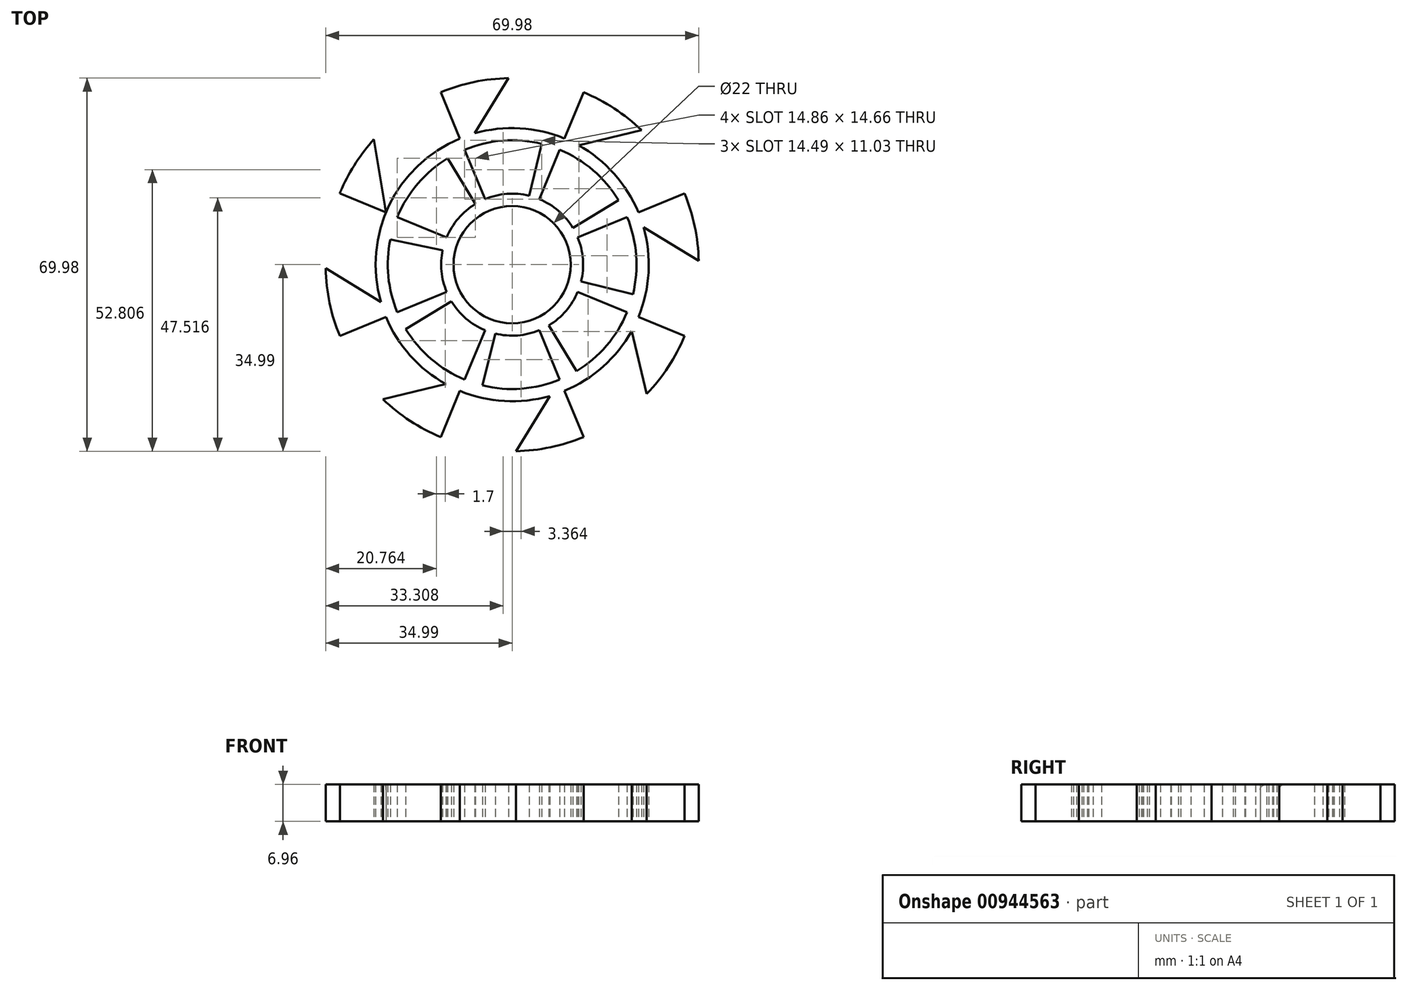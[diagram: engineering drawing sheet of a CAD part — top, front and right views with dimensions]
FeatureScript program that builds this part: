
annotation { "Feature Type Name" : "Feature", "Feature Type Description" : "" }
export const myFeature = defineFeature(function(context is Context, id is Id, definition is map)
    precondition{}
    {
        {
            var Q0;
            Q0=qCreatedBy(makeId("Top.planeOp"),FACE);
            var sketch = newSketch(context, id + "F0", { "sketchPlane" : qUnion([Q0])});
            skCircle(sketch, "E0", {"center": v(0, 0) * mm, "radius": 11 * mm});
            skCircle(sketch, "E1", {"center": v(0, 0) * mm, "radius": 35 * mm});
            skCircle(sketch, "E2", {"center": v(0, 0) * mm, "radius": 13.31 * mm});
            skCircle(sketch, "E3", {"center": v(0, 0) * mm, "radius": 23.33 * mm});
            skCircle(sketch, "E4", {"center": v(0, 0) * mm, "radius": 25.63 * mm});
            skCircle(sketch, "E5.cCircle", {"center": v(0, 0) * mm, "radius": 39.7 * mm, "construction": true});
            skLineSegment(sketch, "E5.0", {"start": v(39.7, 16.44) * mm, "end": v(39.7, -16.44) * mm});
            skLineSegment(sketch, "E5.1", {"start": v(39.7, -16.44) * mm, "end": v(16.44, -39.7) * mm});
            skLineSegment(sketch, "E5.2", {"start": v(16.44, -39.7) * mm, "end": v(-16.44, -39.7) * mm});
            skLineSegment(sketch, "E5.3", {"start": v(-16.44, -39.7) * mm, "end": v(-39.7, -16.44) * mm});
            skLineSegment(sketch, "E5.4", {"start": v(-39.7, -16.44) * mm, "end": v(-39.7, 16.44) * mm});
            skLineSegment(sketch, "E5.5", {"start": v(-39.7, 16.44) * mm, "end": v(-16.44, 39.7) * mm});
            skLineSegment(sketch, "E5.6", {"start": v(-16.44, 39.7) * mm, "end": v(16.44, 39.7) * mm});
            skLineSegment(sketch, "E5.7", {"start": v(16.44, 39.7) * mm, "end": v(39.7, 16.44) * mm});
            skPoint(sketch, "E5.0.midPoint", {"position": v(39.7, 0) * mm});
            skLineSegment(sketch, "E6", {"start": v(0, 0) * mm, "end": v(16.44, 39.7) * mm});
            skLineSegment(sketch, "E7", {"start": v(0, 0) * mm, "end": v(39.7, 16.44) * mm});
            skLineSegment(sketch, "E8", {"start": v(0, 0) * mm, "end": v(39.7, -16.44) * mm});
            skLineSegment(sketch, "E9", {"start": v(-16.44, -39.7) * mm, "end": v(0, 0) * mm});
            skLineSegment(sketch, "E10", {"start": v(-39.7, -16.44) * mm, "end": v(0, 0) * mm});
            skLineSegment(sketch, "E11", {"start": v(-39.7, 16.44) * mm, "end": v(0, 0) * mm});
            skLineSegment(sketch, "E12", {"start": v(-16.44, 39.7) * mm, "end": v(0, 0) * mm});
            skLineSegment(sketch, "E13", {"start": v(16.44, -39.7) * mm, "end": v(0, 0) * mm});
            skLineSegment(sketch, "E14", {"start": v(23.68, 9.8) * mm, "end": v(39.7, 0) * mm});
            skLineSegment(sketch, "E15", {"start": v(23.68, -9.8) * mm, "end": v(28.07, -28.07) * mm});
            skLineSegment(sketch, "E16", {"start": v(9.8, -23.68) * mm, "end": v(0, -39.7) * mm});
            skLineSegment(sketch, "E17", {"start": v(-9.8, -23.68) * mm, "end": v(-28.07, -28.07) * mm});
            skLineSegment(sketch, "E18", {"start": v(-23.68, -9.8) * mm, "end": v(-39.7, 0) * mm});
            skLineSegment(sketch, "E19", {"start": v(-23.68, 9.8) * mm, "end": v(-26.86, 29.22) * mm});
            skLineSegment(sketch, "E20", {"start": v(-9.8, 23.68) * mm, "end": v(0, 39.7) * mm});
            skLineSegment(sketch, "E21", {"start": v(9.8, 23.68) * mm, "end": v(28.07, 28.07) * mm});
            skLineSegment(sketch, "E22", {"start": v(8.93, 21.56) * mm, "end": v(29.6, 26.53) * mm});
            skLineSegment(sketch, "E23", {"start": v(21.56, 8.93) * mm, "end": v(39.63, -2.14) * mm});
            skLineSegment(sketch, "E24", {"start": v(21.56, -8.93) * mm, "end": v(26.5, -29.54) * mm});
            skLineSegment(sketch, "E25", {"start": v(8.93, -21.56) * mm, "end": v(-2.18, -39.7) * mm});
            skLineSegment(sketch, "E26", {"start": v(-8.93, -21.56) * mm, "end": v(-29.54, -26.5) * mm});
            skLineSegment(sketch, "E27", {"start": v(-21.56, -8.93) * mm, "end": v(-39.7, 2.18) * mm});
            skLineSegment(sketch, "E28", {"start": v(-21.56, 8.93) * mm, "end": v(-25.17, 30.97) * mm});
            skLineSegment(sketch, "E29", {"start": v(-8.93, 21.56) * mm, "end": v(2.18, 39.7) * mm});
            skLineSegment(sketch, "E30", {"start": v(0, 39.7) * mm, "end": v(-12.09, 19.96) * mm});
            skLineSegment(sketch, "E31", {"start": v(-12.09, 19.96) * mm, "end": v(0, 0) * mm});
            skLineSegment(sketch, "E32", {"start": v(-26.86, 29.22) * mm, "end": v(-22.85, 4.73) * mm});
            skLineSegment(sketch, "E33", {"start": v(-22.85, 4.73) * mm, "end": v(0, 0) * mm});
            skLineSegment(sketch, "E34", {"start": v(-39.7, 0) * mm, "end": v(-19.96, -12.09) * mm});
            skLineSegment(sketch, "E35", {"start": v(-19.96, -12.09) * mm, "end": v(0, 0) * mm});
            skLineSegment(sketch, "E36", {"start": v(-28.07, -28.07) * mm, "end": v(-5.56, -22.66) * mm});
            skLineSegment(sketch, "E37", {"start": v(-5.56, -22.66) * mm, "end": v(0, 0) * mm});
            skLineSegment(sketch, "E38", {"start": v(0, -39.7) * mm, "end": v(12.09, -19.96) * mm});
            skLineSegment(sketch, "E39", {"start": v(12.09, -19.96) * mm, "end": v(0, 0) * mm});
            skLineSegment(sketch, "E40", {"start": v(28.07, -28.07) * mm, "end": v(22.66, -5.56) * mm});
            skLineSegment(sketch, "E41", {"start": v(22.66, -5.56) * mm, "end": v(0, 0) * mm});
            skLineSegment(sketch, "E42", {"start": v(39.7, 0) * mm, "end": v(19.96, 12.09) * mm});
            skLineSegment(sketch, "E43", {"start": v(19.96, 12.09) * mm, "end": v(0, 0) * mm});
            skLineSegment(sketch, "E44", {"start": v(28.07, 28.07) * mm, "end": v(5.56, 22.66) * mm});
            skLineSegment(sketch, "E45", {"start": v(5.56, 22.66) * mm, "end": v(0, 0) * mm});
            skSolve(sketch);
        }
        {
            var Q0;
            {var subQ0=sQuery(id+"F0.wireOp",EDGE,"E32");var subQ1=sQuery(id+"F0.wireOp",EDGE,"E1");var subQ2=makeQuery(id+"F0.imprint","INTERSECT",VERTEX,{"derivedFrom":[subQ1,subQ0]});Q0=makeQuery(id+"F0.imprint","IMPRINT",FACE,{"disambiguationData":[TD([[makeQuery(id+"F0.imprint","IMPRINT",EDGE,{"disambiguationData":[TD([[subQ2,1.0]])],"derivedFrom":subQ1}),1.0]])]});}
            var Q1;
            {var subQ0=sQuery(id+"F0.wireOp",EDGE,"E29");var subQ5=sQuery(id+"F0.wireOp",EDGE,"E4");var subQ6=makeQuery(id+"F0.imprint","INTERSECT",VERTEX,{"derivedFrom":[subQ5,subQ0]});Q1=makeQuery(id+"F0.imprint","IMPRINT",FACE,{"disambiguationData":[TD([[makeQuery(id+"F0.imprint","IMPRINT",EDGE,{"disambiguationData":[TD([[subQ6,1.0]])],"derivedFrom":subQ5}),1.0]])]});}
            var Q2;
            {var subQ0=sQuery(id+"F0.wireOp",EDGE,"E29");var subQ1=sQuery(id+"F0.wireOp",EDGE,"E1");var subQ2=makeQuery(id+"F0.imprint","INTERSECT",VERTEX,{"derivedFrom":[subQ1,subQ0]});Q2=makeQuery(id+"F0.imprint","IMPRINT",FACE,{"disambiguationData":[TD([[makeQuery(id+"F0.imprint","IMPRINT",EDGE,{"disambiguationData":[TD([[subQ2,-1.0]])],"derivedFrom":subQ1}),1.0]])]});}
            var Q3;
            {var subQ0=sQuery(id+"F0.wireOp",EDGE,"E12");var subQ1=sQuery(id+"F0.wireOp",EDGE,"E3");var subQ2=makeQuery(id+"F0.imprint","INTERSECT",VERTEX,{"derivedFrom":[subQ1,subQ0,sQuery(id+"F0.wireOp",EDGE,"E29")]});Q3=makeQuery(id+"F0.imprint","IMPRINT",FACE,{"disambiguationData":[TD([[makeQuery(id+"F0.imprint","IMPRINT",EDGE,{"disambiguationData":[TD([[subQ2,-1.0]])],"derivedFrom":subQ1}),-1.0]])]});}
            var Q4;
            {var subQ0=sQuery(id+"F0.wireOp",EDGE,"E28");var subQ5=sQuery(id+"F0.wireOp",EDGE,"E4");var subQ6=makeQuery(id+"F0.imprint","INTERSECT",VERTEX,{"derivedFrom":[subQ5,subQ0]});Q4=makeQuery(id+"F0.imprint","IMPRINT",FACE,{"disambiguationData":[TD([[makeQuery(id+"F0.imprint","IMPRINT",EDGE,{"disambiguationData":[TD([[subQ6,1.0]])],"derivedFrom":subQ5}),1.0]])]});}
            var Q5;
            {var subQ0=sQuery(id+"F0.wireOp",EDGE,"E29");var subQ1=sQuery(id+"F0.wireOp",EDGE,"E4");var subQ2=makeQuery(id+"F0.imprint","INTERSECT",VERTEX,{"derivedFrom":[subQ1,subQ0]});Q5=makeQuery(id+"F0.imprint","IMPRINT",FACE,{"disambiguationData":[TD([[makeQuery(id+"F0.imprint","IMPRINT",EDGE,{"disambiguationData":[TD([[subQ2,-1.0]])],"derivedFrom":subQ1}),1.0]])]});}
            var Q6;
            {var subQ0=sQuery(id+"F0.wireOp",EDGE,"E28");var subQ1=sQuery(id+"F0.wireOp",EDGE,"E4");var subQ2=makeQuery(id+"F0.imprint","INTERSECT",VERTEX,{"derivedFrom":[subQ1,subQ0]});Q6=makeQuery(id+"F0.imprint","IMPRINT",FACE,{"disambiguationData":[TD([[makeQuery(id+"F0.imprint","IMPRINT",EDGE,{"disambiguationData":[TD([[subQ2,-1.0]])],"derivedFrom":subQ1}),1.0]])]});}
            var Q7;
            {var subQ0=sQuery(id+"F0.wireOp",EDGE,"E11");var subQ1=sQuery(id+"F0.wireOp",EDGE,"E3");var subQ2=makeQuery(id+"F0.imprint","INTERSECT",VERTEX,{"derivedFrom":[subQ1,subQ0,sQuery(id+"F0.wireOp",EDGE,"E28")]});Q7=makeQuery(id+"F0.imprint","IMPRINT",FACE,{"disambiguationData":[TD([[makeQuery(id+"F0.imprint","IMPRINT",EDGE,{"disambiguationData":[TD([[subQ2,-1.0]])],"derivedFrom":subQ1}),-1.0]])]});}
            var Q8;
            {var subQ0=sQuery(id+"F0.wireOp",EDGE,"E27");var subQ5=sQuery(id+"F0.wireOp",EDGE,"E4");var subQ6=makeQuery(id+"F0.imprint","INTERSECT",VERTEX,{"derivedFrom":[subQ5,subQ0]});Q8=makeQuery(id+"F0.imprint","IMPRINT",FACE,{"disambiguationData":[TD([[makeQuery(id+"F0.imprint","IMPRINT",EDGE,{"disambiguationData":[TD([[subQ6,1.0]])],"derivedFrom":subQ5}),1.0]])]});}
            var Q9;
            {var subQ0=sQuery(id+"F0.wireOp",EDGE,"E27");var subQ1=sQuery(id+"F0.wireOp",EDGE,"E4");var subQ2=makeQuery(id+"F0.imprint","INTERSECT",VERTEX,{"derivedFrom":[subQ1,subQ0]});Q9=makeQuery(id+"F0.imprint","IMPRINT",FACE,{"disambiguationData":[TD([[makeQuery(id+"F0.imprint","IMPRINT",EDGE,{"disambiguationData":[TD([[subQ2,-1.0]])],"derivedFrom":subQ1}),1.0]])]});}
            var Q10;
            {var subQ0=sQuery(id+"F0.wireOp",EDGE,"E10");var subQ1=sQuery(id+"F0.wireOp",EDGE,"E3");var subQ2=makeQuery(id+"F0.imprint","INTERSECT",VERTEX,{"derivedFrom":[subQ1,subQ0,sQuery(id+"F0.wireOp",EDGE,"E27")]});Q10=makeQuery(id+"F0.imprint","IMPRINT",FACE,{"disambiguationData":[TD([[makeQuery(id+"F0.imprint","IMPRINT",EDGE,{"disambiguationData":[TD([[subQ2,-1.0]])],"derivedFrom":subQ1}),-1.0]])]});}
            var Q11;
            {var subQ0=sQuery(id+"F0.wireOp",EDGE,"E26");var subQ5=sQuery(id+"F0.wireOp",EDGE,"E4");var subQ7=makeQuery(id+"F0.imprint","INTERSECT",VERTEX,{"derivedFrom":[subQ5,subQ0]});Q11=makeQuery(id+"F0.imprint","IMPRINT",FACE,{"disambiguationData":[TD([[makeQuery(id+"F0.imprint","IMPRINT",EDGE,{"disambiguationData":[TD([[subQ7,1.0]])],"derivedFrom":subQ5}),1.0]])]});}
            var Q12;
            {var subQ0=sQuery(id+"F0.wireOp",EDGE,"E9");var subQ1=sQuery(id+"F0.wireOp",EDGE,"E3");var subQ2=makeQuery(id+"F0.imprint","INTERSECT",VERTEX,{"derivedFrom":[subQ1,subQ0,sQuery(id+"F0.wireOp",EDGE,"E26")]});Q12=makeQuery(id+"F0.imprint","IMPRINT",FACE,{"disambiguationData":[TD([[makeQuery(id+"F0.imprint","IMPRINT",EDGE,{"disambiguationData":[TD([[subQ2,-1.0]])],"derivedFrom":subQ1}),-1.0]])]});}
            var Q13;
            {var subQ0=sQuery(id+"F0.wireOp",EDGE,"E26");var subQ1=sQuery(id+"F0.wireOp",EDGE,"E4");var subQ2=makeQuery(id+"F0.imprint","INTERSECT",VERTEX,{"derivedFrom":[subQ1,subQ0]});Q13=makeQuery(id+"F0.imprint","IMPRINT",FACE,{"disambiguationData":[TD([[makeQuery(id+"F0.imprint","IMPRINT",EDGE,{"disambiguationData":[TD([[subQ2,-1.0]])],"derivedFrom":subQ1}),1.0]])]});}
            var Q14;
            {var subQ0=sQuery(id+"F0.wireOp",EDGE,"E25");var subQ5=sQuery(id+"F0.wireOp",EDGE,"E4");var subQ6=makeQuery(id+"F0.imprint","INTERSECT",VERTEX,{"derivedFrom":[subQ5,subQ0]});Q14=makeQuery(id+"F0.imprint","IMPRINT",FACE,{"disambiguationData":[TD([[makeQuery(id+"F0.imprint","IMPRINT",EDGE,{"disambiguationData":[TD([[subQ6,1.0]])],"derivedFrom":subQ5}),1.0]])]});}
            var Q15;
            {var subQ0=sQuery(id+"F0.wireOp",EDGE,"E25");var subQ1=sQuery(id+"F0.wireOp",EDGE,"E4");var subQ2=makeQuery(id+"F0.imprint","INTERSECT",VERTEX,{"derivedFrom":[subQ1,subQ0]});Q15=makeQuery(id+"F0.imprint","IMPRINT",FACE,{"disambiguationData":[TD([[makeQuery(id+"F0.imprint","IMPRINT",EDGE,{"disambiguationData":[TD([[subQ2,-1.0]])],"derivedFrom":subQ1}),1.0]])]});}
            var Q16;
            {var subQ0=sQuery(id+"F0.wireOp",EDGE,"E13");var subQ1=sQuery(id+"F0.wireOp",EDGE,"E3");var subQ2=makeQuery(id+"F0.imprint","INTERSECT",VERTEX,{"derivedFrom":[subQ1,subQ0,sQuery(id+"F0.wireOp",EDGE,"E25")]});Q16=makeQuery(id+"F0.imprint","IMPRINT",FACE,{"disambiguationData":[TD([[makeQuery(id+"F0.imprint","IMPRINT",EDGE,{"disambiguationData":[TD([[subQ2,-1.0]])],"derivedFrom":subQ1}),-1.0]])]});}
            var Q17;
            {var subQ0=sQuery(id+"F0.wireOp",EDGE,"E24");var subQ5=sQuery(id+"F0.wireOp",EDGE,"E4");var subQ6=makeQuery(id+"F0.imprint","INTERSECT",VERTEX,{"derivedFrom":[subQ5,subQ0]});Q17=makeQuery(id+"F0.imprint","IMPRINT",FACE,{"disambiguationData":[TD([[makeQuery(id+"F0.imprint","IMPRINT",EDGE,{"disambiguationData":[TD([[subQ6,1.0]])],"derivedFrom":subQ5}),1.0]])]});}
            var Q18;
            {var subQ0=sQuery(id+"F0.wireOp",EDGE,"E8");var subQ1=sQuery(id+"F0.wireOp",EDGE,"E3");var subQ2=makeQuery(id+"F0.imprint","INTERSECT",VERTEX,{"derivedFrom":[subQ1,subQ0,sQuery(id+"F0.wireOp",EDGE,"E24")]});Q18=makeQuery(id+"F0.imprint","IMPRINT",FACE,{"disambiguationData":[TD([[makeQuery(id+"F0.imprint","IMPRINT",EDGE,{"disambiguationData":[TD([[subQ2,-1.0]])],"derivedFrom":subQ1}),-1.0]])]});}
            var Q19;
            {var subQ0=sQuery(id+"F0.wireOp",EDGE,"E24");var subQ1=sQuery(id+"F0.wireOp",EDGE,"E4");var subQ2=makeQuery(id+"F0.imprint","INTERSECT",VERTEX,{"derivedFrom":[subQ1,subQ0]});Q19=makeQuery(id+"F0.imprint","IMPRINT",FACE,{"disambiguationData":[TD([[makeQuery(id+"F0.imprint","IMPRINT",EDGE,{"disambiguationData":[TD([[subQ2,-1.0]])],"derivedFrom":subQ1}),1.0]])]});}
            var Q20;
            {var subQ0=sQuery(id+"F0.wireOp",EDGE,"E23");var subQ5=sQuery(id+"F0.wireOp",EDGE,"E4");var subQ6=makeQuery(id+"F0.imprint","INTERSECT",VERTEX,{"derivedFrom":[subQ5,subQ0]});Q20=makeQuery(id+"F0.imprint","IMPRINT",FACE,{"disambiguationData":[TD([[makeQuery(id+"F0.imprint","IMPRINT",EDGE,{"disambiguationData":[TD([[subQ6,1.0]])],"derivedFrom":subQ5}),1.0]])]});}
            var Q21;
            {var subQ0=sQuery(id+"F0.wireOp",EDGE,"E23");var subQ1=sQuery(id+"F0.wireOp",EDGE,"E4");var subQ2=makeQuery(id+"F0.imprint","INTERSECT",VERTEX,{"derivedFrom":[subQ1,subQ0]});Q21=makeQuery(id+"F0.imprint","IMPRINT",FACE,{"disambiguationData":[TD([[makeQuery(id+"F0.imprint","IMPRINT",EDGE,{"disambiguationData":[TD([[subQ2,-1.0]])],"derivedFrom":subQ1}),1.0]])]});}
            var Q22;
            {var subQ0=sQuery(id+"F0.wireOp",EDGE,"E7");var subQ1=sQuery(id+"F0.wireOp",EDGE,"E3");var subQ2=makeQuery(id+"F0.imprint","INTERSECT",VERTEX,{"derivedFrom":[subQ1,subQ0,sQuery(id+"F0.wireOp",EDGE,"E23")]});Q22=makeQuery(id+"F0.imprint","IMPRINT",FACE,{"disambiguationData":[TD([[makeQuery(id+"F0.imprint","IMPRINT",EDGE,{"disambiguationData":[TD([[subQ2,-1.0]])],"derivedFrom":subQ1}),-1.0]])]});}
            var Q23;
            {var subQ0=sQuery(id+"F0.wireOp",EDGE,"E22");var subQ5=sQuery(id+"F0.wireOp",EDGE,"E4");var subQ6=makeQuery(id+"F0.imprint","INTERSECT",VERTEX,{"derivedFrom":[subQ5,subQ0]});Q23=makeQuery(id+"F0.imprint","IMPRINT",FACE,{"disambiguationData":[TD([[makeQuery(id+"F0.imprint","IMPRINT",EDGE,{"disambiguationData":[TD([[subQ6,1.0]])],"derivedFrom":subQ5}),1.0]])]});}
            var Q24;
            {var subQ0=sQuery(id+"F0.wireOp",EDGE,"E22");var subQ1=sQuery(id+"F0.wireOp",EDGE,"E4");var subQ2=makeQuery(id+"F0.imprint","INTERSECT",VERTEX,{"derivedFrom":[subQ1,subQ0]});Q24=makeQuery(id+"F0.imprint","IMPRINT",FACE,{"disambiguationData":[TD([[makeQuery(id+"F0.imprint","IMPRINT",EDGE,{"disambiguationData":[TD([[subQ2,-1.0]])],"derivedFrom":subQ1}),1.0]])]});}
            var Q25;
            {var subQ0=sQuery(id+"F0.wireOp",EDGE,"E6");var subQ1=sQuery(id+"F0.wireOp",EDGE,"E3");var subQ2=makeQuery(id+"F0.imprint","INTERSECT",VERTEX,{"derivedFrom":[subQ1,subQ0,sQuery(id+"F0.wireOp",EDGE,"E22")]});Q25=makeQuery(id+"F0.imprint","IMPRINT",FACE,{"disambiguationData":[TD([[makeQuery(id+"F0.imprint","IMPRINT",EDGE,{"disambiguationData":[TD([[subQ2,-1.0]])],"derivedFrom":subQ1}),-1.0]])]});}
            var Q26;
            {var subQ0=sQuery(id+"F0.wireOp",EDGE,"E22");var subQ1=sQuery(id+"F0.wireOp",EDGE,"E1");var subQ2=makeQuery(id+"F0.imprint","INTERSECT",VERTEX,{"derivedFrom":[subQ1,subQ0]});Q26=makeQuery(id+"F0.imprint","IMPRINT",FACE,{"disambiguationData":[TD([[makeQuery(id+"F0.imprint","IMPRINT",EDGE,{"disambiguationData":[TD([[subQ2,-1.0]])],"derivedFrom":subQ1}),1.0]])]});}
            var Q27;
            {var subQ0=sQuery(id+"F0.wireOp",EDGE,"E23");var subQ1=sQuery(id+"F0.wireOp",EDGE,"E1");var subQ2=makeQuery(id+"F0.imprint","INTERSECT",VERTEX,{"derivedFrom":[subQ1,subQ0]});Q27=makeQuery(id+"F0.imprint","IMPRINT",FACE,{"disambiguationData":[TD([[makeQuery(id+"F0.imprint","IMPRINT",EDGE,{"disambiguationData":[TD([[subQ2,-1.0]])],"derivedFrom":subQ1}),1.0]])]});}
            var Q28;
            {var subQ0=sQuery(id+"F0.wireOp",EDGE,"E24");var subQ1=sQuery(id+"F0.wireOp",EDGE,"E1");var subQ2=makeQuery(id+"F0.imprint","INTERSECT",VERTEX,{"derivedFrom":[subQ1,subQ0]});Q28=makeQuery(id+"F0.imprint","IMPRINT",FACE,{"disambiguationData":[TD([[makeQuery(id+"F0.imprint","IMPRINT",EDGE,{"disambiguationData":[TD([[subQ2,-1.0]])],"derivedFrom":subQ1}),1.0]])]});}
            var Q29;
            {var subQ0=sQuery(id+"F0.wireOp",EDGE,"E25");var subQ1=sQuery(id+"F0.wireOp",EDGE,"E1");var subQ2=makeQuery(id+"F0.imprint","INTERSECT",VERTEX,{"derivedFrom":[subQ1,subQ0]});Q29=makeQuery(id+"F0.imprint","IMPRINT",FACE,{"disambiguationData":[TD([[makeQuery(id+"F0.imprint","IMPRINT",EDGE,{"disambiguationData":[TD([[subQ2,-1.0]])],"derivedFrom":subQ1}),1.0]])]});}
            var Q30;
            {var subQ0=sQuery(id+"F0.wireOp",EDGE,"E27");var subQ1=sQuery(id+"F0.wireOp",EDGE,"E1");var subQ2=makeQuery(id+"F0.imprint","INTERSECT",VERTEX,{"derivedFrom":[subQ1,subQ0]});Q30=makeQuery(id+"F0.imprint","IMPRINT",FACE,{"disambiguationData":[TD([[makeQuery(id+"F0.imprint","IMPRINT",EDGE,{"disambiguationData":[TD([[subQ2,-1.0]])],"derivedFrom":subQ1}),1.0]])]});}
            var Q31;
            {var subQ0=sQuery(id+"F0.wireOp",EDGE,"E26");var subQ1=sQuery(id+"F0.wireOp",EDGE,"E1");var subQ2=makeQuery(id+"F0.imprint","INTERSECT",VERTEX,{"derivedFrom":[subQ1,subQ0]});Q31=makeQuery(id+"F0.imprint","IMPRINT",FACE,{"disambiguationData":[TD([[makeQuery(id+"F0.imprint","IMPRINT",EDGE,{"disambiguationData":[TD([[subQ2,-1.0]])],"derivedFrom":subQ1}),1.0]])]});}
            var Q32;
            {var subQ0=sQuery(id+"F0.wireOp",EDGE,"E13");var subQ1=sQuery(id+"F0.wireOp",EDGE,"E2");var subQ2=makeQuery(id+"F0.imprint","INTERSECT",VERTEX,{"derivedFrom":[subQ1,subQ0]});Q32=makeQuery(id+"F0.imprint","IMPRINT",FACE,{"disambiguationData":[TD([[makeQuery(id+"F0.imprint","IMPRINT",EDGE,{"disambiguationData":[TD([[subQ2,-1.0]])],"derivedFrom":subQ1}),-1.0]])]});}
            var Q33;
            {var subQ0=sQuery(id+"F0.wireOp",EDGE,"E12");var subQ1=sQuery(id+"F0.wireOp",EDGE,"E2");var subQ2=makeQuery(id+"F0.imprint","INTERSECT",VERTEX,{"derivedFrom":[subQ1,subQ0]});Q33=makeQuery(id+"F0.imprint","IMPRINT",FACE,{"disambiguationData":[TD([[makeQuery(id+"F0.imprint","IMPRINT",EDGE,{"disambiguationData":[TD([[subQ2,-1.0]])],"derivedFrom":subQ1}),-1.0]])]});}
            var Q34;
            {var subQ0=sQuery(id+"F0.wireOp",EDGE,"E6");var subQ1=sQuery(id+"F0.wireOp",EDGE,"E2");var subQ2=makeQuery(id+"F0.imprint","INTERSECT",VERTEX,{"derivedFrom":[subQ1,subQ0]});Q34=makeQuery(id+"F0.imprint","IMPRINT",FACE,{"disambiguationData":[TD([[makeQuery(id+"F0.imprint","IMPRINT",EDGE,{"disambiguationData":[TD([[subQ2,-1.0]])],"derivedFrom":subQ1}),-1.0]])]});}
            var Q35;
            {var subQ0=sQuery(id+"F0.wireOp",EDGE,"E45");var subQ1=sQuery(id+"F0.wireOp",EDGE,"E0");var subQ2=makeQuery(id+"F0.imprint","INTERSECT",VERTEX,{"derivedFrom":[subQ1,subQ0]});Q35=makeQuery(id+"F0.imprint","IMPRINT",FACE,{"disambiguationData":[TD([[makeQuery(id+"F0.imprint","IMPRINT",EDGE,{"disambiguationData":[TD([[subQ2,-1.0]])],"derivedFrom":subQ1}),-1.0]])]});}
            var Q36;
            {var subQ0=sQuery(id+"F0.wireOp",EDGE,"E12");var subQ1=sQuery(id+"F0.wireOp",EDGE,"E0");var subQ2=makeQuery(id+"F0.imprint","INTERSECT",VERTEX,{"derivedFrom":[subQ1,subQ0]});Q36=makeQuery(id+"F0.imprint","IMPRINT",FACE,{"disambiguationData":[TD([[makeQuery(id+"F0.imprint","IMPRINT",EDGE,{"disambiguationData":[TD([[subQ2,-1.0]])],"derivedFrom":subQ1}),-1.0]])]});}
            var Q37;
            {var subQ0=sQuery(id+"F0.wireOp",EDGE,"E11");var subQ1=sQuery(id+"F0.wireOp",EDGE,"E0");var subQ2=makeQuery(id+"F0.imprint","INTERSECT",VERTEX,{"derivedFrom":[subQ1,subQ0]});Q37=makeQuery(id+"F0.imprint","IMPRINT",FACE,{"disambiguationData":[TD([[makeQuery(id+"F0.imprint","IMPRINT",EDGE,{"disambiguationData":[TD([[subQ2,-1.0]])],"derivedFrom":subQ1}),-1.0]])]});}
            var Q38;
            {var subQ0=sQuery(id+"F0.wireOp",EDGE,"E31");var subQ1=sQuery(id+"F0.wireOp",EDGE,"E0");var subQ2=makeQuery(id+"F0.imprint","INTERSECT",VERTEX,{"derivedFrom":[subQ1,subQ0]});Q38=makeQuery(id+"F0.imprint","IMPRINT",FACE,{"disambiguationData":[TD([[makeQuery(id+"F0.imprint","IMPRINT",EDGE,{"disambiguationData":[TD([[subQ2,-1.0]])],"derivedFrom":subQ1}),-1.0]])]});}
            var Q39;
            {var subQ0=sQuery(id+"F0.wireOp",EDGE,"E33");var subQ1=sQuery(id+"F0.wireOp",EDGE,"E0");var subQ2=makeQuery(id+"F0.imprint","INTERSECT",VERTEX,{"derivedFrom":[subQ1,subQ0]});Q39=makeQuery(id+"F0.imprint","IMPRINT",FACE,{"disambiguationData":[TD([[makeQuery(id+"F0.imprint","IMPRINT",EDGE,{"disambiguationData":[TD([[subQ2,-1.0]])],"derivedFrom":subQ1}),-1.0]])]});}
            var Q40;
            {var subQ0=sQuery(id+"F0.wireOp",EDGE,"E35");var subQ1=sQuery(id+"F0.wireOp",EDGE,"E0");var subQ2=makeQuery(id+"F0.imprint","INTERSECT",VERTEX,{"derivedFrom":[subQ1,subQ0]});Q40=makeQuery(id+"F0.imprint","IMPRINT",FACE,{"disambiguationData":[TD([[makeQuery(id+"F0.imprint","IMPRINT",EDGE,{"disambiguationData":[TD([[subQ2,-1.0]])],"derivedFrom":subQ1}),-1.0]])]});}
            var Q41;
            {var subQ0=sQuery(id+"F0.wireOp",EDGE,"E37");var subQ1=sQuery(id+"F0.wireOp",EDGE,"E0");var subQ2=makeQuery(id+"F0.imprint","INTERSECT",VERTEX,{"derivedFrom":[subQ1,subQ0]});Q41=makeQuery(id+"F0.imprint","IMPRINT",FACE,{"disambiguationData":[TD([[makeQuery(id+"F0.imprint","IMPRINT",EDGE,{"disambiguationData":[TD([[subQ2,-1.0]])],"derivedFrom":subQ1}),-1.0]])]});}
            var Q42;
            {var subQ0=sQuery(id+"F0.wireOp",EDGE,"E39");var subQ1=sQuery(id+"F0.wireOp",EDGE,"E0");var subQ2=makeQuery(id+"F0.imprint","INTERSECT",VERTEX,{"derivedFrom":[subQ1,subQ0]});Q42=makeQuery(id+"F0.imprint","IMPRINT",FACE,{"disambiguationData":[TD([[makeQuery(id+"F0.imprint","IMPRINT",EDGE,{"disambiguationData":[TD([[subQ2,-1.0]])],"derivedFrom":subQ1}),-1.0]])]});}
            var Q43;
            {var subQ0=sQuery(id+"F0.wireOp",EDGE,"E7");var subQ1=sQuery(id+"F0.wireOp",EDGE,"E0");var subQ2=makeQuery(id+"F0.imprint","INTERSECT",VERTEX,{"derivedFrom":[subQ1,subQ0]});Q43=makeQuery(id+"F0.imprint","IMPRINT",FACE,{"disambiguationData":[TD([[makeQuery(id+"F0.imprint","IMPRINT",EDGE,{"disambiguationData":[TD([[subQ2,1.0]])],"derivedFrom":subQ1}),-1.0]])]});}
            var Q44;
            {var subQ0=sQuery(id+"F0.wireOp",EDGE,"E43");var subQ1=sQuery(id+"F0.wireOp",EDGE,"E0");var subQ2=makeQuery(id+"F0.imprint","INTERSECT",VERTEX,{"derivedFrom":[subQ1,subQ0]});Q44=makeQuery(id+"F0.imprint","IMPRINT",FACE,{"disambiguationData":[TD([[makeQuery(id+"F0.imprint","IMPRINT",EDGE,{"disambiguationData":[TD([[subQ2,-1.0]])],"derivedFrom":subQ1}),-1.0]])]});}
            var Q45;
            {var subQ0=sQuery(id+"F0.wireOp",EDGE,"E6");var subQ1=sQuery(id+"F0.wireOp",EDGE,"E0");var subQ2=makeQuery(id+"F0.imprint","INTERSECT",VERTEX,{"derivedFrom":[subQ1,subQ0]});Q45=makeQuery(id+"F0.imprint","IMPRINT",FACE,{"disambiguationData":[TD([[makeQuery(id+"F0.imprint","IMPRINT",EDGE,{"disambiguationData":[TD([[subQ2,-1.0]])],"derivedFrom":subQ1}),-1.0]])]});}
            var Q46;
            {var subQ0=sQuery(id+"F0.wireOp",EDGE,"E43");var subQ1=sQuery(id+"F0.wireOp",EDGE,"E0");var subQ2=makeQuery(id+"F0.imprint","INTERSECT",VERTEX,{"derivedFrom":[subQ1,subQ0]});Q46=makeQuery(id+"F0.imprint","IMPRINT",FACE,{"disambiguationData":[TD([[makeQuery(id+"F0.imprint","IMPRINT",EDGE,{"disambiguationData":[TD([[subQ2,1.0]])],"derivedFrom":subQ1}),-1.0]])]});}
            var Q47;
            {var subQ0=sQuery(id+"F0.wireOp",EDGE,"E8");var subQ1=sQuery(id+"F0.wireOp",EDGE,"E0");var subQ2=makeQuery(id+"F0.imprint","INTERSECT",VERTEX,{"derivedFrom":[subQ1,subQ0]});Q47=makeQuery(id+"F0.imprint","IMPRINT",FACE,{"disambiguationData":[TD([[makeQuery(id+"F0.imprint","IMPRINT",EDGE,{"disambiguationData":[TD([[subQ2,-1.0]])],"derivedFrom":subQ1}),-1.0]])]});}
            var Q48;
            {var subQ0=sQuery(id+"F0.wireOp",EDGE,"E13");var subQ1=sQuery(id+"F0.wireOp",EDGE,"E0");var subQ2=makeQuery(id+"F0.imprint","INTERSECT",VERTEX,{"derivedFrom":[subQ1,subQ0]});Q48=makeQuery(id+"F0.imprint","IMPRINT",FACE,{"disambiguationData":[TD([[makeQuery(id+"F0.imprint","IMPRINT",EDGE,{"disambiguationData":[TD([[subQ2,-1.0]])],"derivedFrom":subQ1}),-1.0]])]});}
            var Q49;
            {var subQ0=sQuery(id+"F0.wireOp",EDGE,"E9");var subQ1=sQuery(id+"F0.wireOp",EDGE,"E0");var subQ2=makeQuery(id+"F0.imprint","INTERSECT",VERTEX,{"derivedFrom":[subQ1,subQ0]});Q49=makeQuery(id+"F0.imprint","IMPRINT",FACE,{"disambiguationData":[TD([[makeQuery(id+"F0.imprint","IMPRINT",EDGE,{"disambiguationData":[TD([[subQ2,-1.0]])],"derivedFrom":subQ1}),-1.0]])]});}
            var Q50;
            {var subQ0=sQuery(id+"F0.wireOp",EDGE,"E10");var subQ1=sQuery(id+"F0.wireOp",EDGE,"E0");var subQ2=makeQuery(id+"F0.imprint","INTERSECT",VERTEX,{"derivedFrom":[subQ1,subQ0]});Q50=makeQuery(id+"F0.imprint","IMPRINT",FACE,{"disambiguationData":[TD([[makeQuery(id+"F0.imprint","IMPRINT",EDGE,{"disambiguationData":[TD([[subQ2,-1.0]])],"derivedFrom":subQ1}),-1.0]])]});}
            var Q51;
            {var subQ0=sQuery(id+"F0.wireOp",EDGE,"E9");var subQ1=sQuery(id+"F0.wireOp",EDGE,"E2");var subQ2=makeQuery(id+"F0.imprint","INTERSECT",VERTEX,{"derivedFrom":[subQ1,subQ0]});Q51=makeQuery(id+"F0.imprint","IMPRINT",FACE,{"disambiguationData":[TD([[makeQuery(id+"F0.imprint","IMPRINT",EDGE,{"disambiguationData":[TD([[subQ2,-1.0]])],"derivedFrom":subQ1}),-1.0]])]});}
            var Q52;
            {var subQ0=sQuery(id+"F0.wireOp",EDGE,"E10");var subQ1=sQuery(id+"F0.wireOp",EDGE,"E2");var subQ2=makeQuery(id+"F0.imprint","INTERSECT",VERTEX,{"derivedFrom":[subQ1,subQ0]});Q52=makeQuery(id+"F0.imprint","IMPRINT",FACE,{"disambiguationData":[TD([[makeQuery(id+"F0.imprint","IMPRINT",EDGE,{"disambiguationData":[TD([[subQ2,-1.0]])],"derivedFrom":subQ1}),-1.0]])]});}
            var Q53;
            {var subQ0=sQuery(id+"F0.wireOp",EDGE,"E11");var subQ1=sQuery(id+"F0.wireOp",EDGE,"E2");var subQ2=makeQuery(id+"F0.imprint","INTERSECT",VERTEX,{"derivedFrom":[subQ1,subQ0]});Q53=makeQuery(id+"F0.imprint","IMPRINT",FACE,{"disambiguationData":[TD([[makeQuery(id+"F0.imprint","IMPRINT",EDGE,{"disambiguationData":[TD([[subQ2,-1.0]])],"derivedFrom":subQ1}),-1.0]])]});}
            var Q54;
            {var subQ0=sQuery(id+"F0.wireOp",EDGE,"E8");var subQ1=sQuery(id+"F0.wireOp",EDGE,"E2");var subQ2=makeQuery(id+"F0.imprint","INTERSECT",VERTEX,{"derivedFrom":[subQ1,subQ0]});Q54=makeQuery(id+"F0.imprint","IMPRINT",FACE,{"disambiguationData":[TD([[makeQuery(id+"F0.imprint","IMPRINT",EDGE,{"disambiguationData":[TD([[subQ2,-1.0]])],"derivedFrom":subQ1}),-1.0]])]});}
            var Q55;
            {var subQ0=sQuery(id+"F0.wireOp",EDGE,"E43");var subQ1=sQuery(id+"F0.wireOp",EDGE,"E2");var subQ2=makeQuery(id+"F0.imprint","INTERSECT",VERTEX,{"derivedFrom":[subQ1,subQ0]});Q55=makeQuery(id+"F0.imprint","IMPRINT",FACE,{"disambiguationData":[TD([[makeQuery(id+"F0.imprint","IMPRINT",EDGE,{"disambiguationData":[TD([[subQ2,1.0]])],"derivedFrom":subQ1}),-1.0]])]});}
            extrude(context, id + "F1", {"entities" : qUnion([Q0, Q1, Q2, Q3, Q4, Q5, Q6, Q7, Q8, Q9, Q10, Q11, Q12, Q13, Q14, Q15, Q16, Q17, Q18, Q19, Q20, Q21, Q22, Q23, Q24, Q25, Q26, Q27, Q28, Q29, Q30, Q31, Q32, Q33, Q34, Q35, Q36, Q37, Q38, Q39, Q40, Q41, Q42, Q43, Q44, Q45, Q46, Q47, Q48, Q49, Q50, Q51, Q52, Q53, Q54, Q55]), "depth" : 6.96 * mm, "offsetDistance" : 25 * mm});
        }
        {
            var Q0;
            {var subQ0=sQuery(id+"F0.wireOp",EDGE,"E2");Q0=makeQuery(id+"F1.opExtrude","CAP_EDGE",EDGE,{"disambiguationData":[OSD([subQ0]),TDD([makeQuery(id+"F0.imprint","IMPRINT",EDGE,{"disambiguationData":[TD([[makeQuery(id+"F0.imprint","INTERSECT",VERTEX,{"derivedFrom":[subQ0,sQuery(id+"F0.wireOp",EDGE,"E43")]}),-1.0]])],"derivedFrom":subQ0})])],"isStart":false});}
            var Q1;
            {var subQ0=sQuery(id+"F0.wireOp",EDGE,"E2");Q1=makeQuery(id+"F1.opExtrude","CAP_EDGE",EDGE,{"disambiguationData":[OSD([subQ0]),TDD([makeQuery(id+"F0.imprint","IMPRINT",EDGE,{"disambiguationData":[TD([[makeQuery(id+"F0.imprint","INTERSECT",VERTEX,{"derivedFrom":[subQ0,sQuery(id+"F0.wireOp",EDGE,"E7")]}),1.0]])],"derivedFrom":subQ0})])],"isStart":false});}
            var Q2;
            {var subQ0=sQuery(id+"F0.wireOp",EDGE,"E2");Q2=makeQuery(id+"F1.opExtrude","CAP_EDGE",EDGE,{"disambiguationData":[OSD([subQ0]),TDD([makeQuery(id+"F0.imprint","IMPRINT",EDGE,{"disambiguationData":[TD([[makeQuery(id+"F0.imprint","INTERSECT",VERTEX,{"derivedFrom":[subQ0,sQuery(id+"F0.wireOp",EDGE,"E39")]}),-1.0]])],"derivedFrom":subQ0})])],"isStart":false});}
            var Q3;
            {var subQ0=sQuery(id+"F0.wireOp",EDGE,"E2");Q3=makeQuery(id+"F1.opExtrude","CAP_EDGE",EDGE,{"disambiguationData":[OSD([subQ0]),TDD([makeQuery(id+"F0.imprint","IMPRINT",EDGE,{"disambiguationData":[TD([[makeQuery(id+"F0.imprint","INTERSECT",VERTEX,{"derivedFrom":[subQ0,sQuery(id+"F0.wireOp",EDGE,"E37")]}),-1.0]])],"derivedFrom":subQ0})])],"isStart":false});}
            var Q4;
            {var subQ0=sQuery(id+"F0.wireOp",EDGE,"E2");Q4=makeQuery(id+"F1.opExtrude","CAP_EDGE",EDGE,{"disambiguationData":[OSD([subQ0]),TDD([makeQuery(id+"F0.imprint","IMPRINT",EDGE,{"disambiguationData":[TD([[makeQuery(id+"F0.imprint","INTERSECT",VERTEX,{"derivedFrom":[subQ0,sQuery(id+"F0.wireOp",EDGE,"E35")]}),-1.0]])],"derivedFrom":subQ0})])],"isStart":false});}
            var Q5;
            {var subQ0=sQuery(id+"F0.wireOp",EDGE,"E2");Q5=makeQuery(id+"F1.opExtrude","CAP_EDGE",EDGE,{"disambiguationData":[OSD([subQ0]),TDD([makeQuery(id+"F0.imprint","IMPRINT",EDGE,{"disambiguationData":[TD([[makeQuery(id+"F0.imprint","INTERSECT",VERTEX,{"derivedFrom":[subQ0,sQuery(id+"F0.wireOp",EDGE,"E33")]}),-1.0]])],"derivedFrom":subQ0})])],"isStart":false});}
            var Q6;
            {var subQ0=sQuery(id+"F0.wireOp",EDGE,"E2");Q6=makeQuery(id+"F1.opExtrude","CAP_EDGE",EDGE,{"disambiguationData":[OSD([subQ0]),TDD([makeQuery(id+"F0.imprint","IMPRINT",EDGE,{"disambiguationData":[TD([[makeQuery(id+"F0.imprint","INTERSECT",VERTEX,{"derivedFrom":[subQ0,sQuery(id+"F0.wireOp",EDGE,"E31")]}),-1.0]])],"derivedFrom":subQ0})])],"isStart":false});}
            var Q7;
            {var subQ0=sQuery(id+"F0.wireOp",EDGE,"E2");Q7=makeQuery(id+"F1.opExtrude","CAP_EDGE",EDGE,{"disambiguationData":[OSD([subQ0]),TDD([makeQuery(id+"F0.imprint","IMPRINT",EDGE,{"disambiguationData":[TD([[makeQuery(id+"F0.imprint","INTERSECT",VERTEX,{"derivedFrom":[subQ0,sQuery(id+"F0.wireOp",EDGE,"E45")]}),-1.0]])],"derivedFrom":subQ0})])],"isStart":false});}
            var Q8;
            Q8=makeQuery(id+"F1.opExtrude","CAP_EDGE",EDGE,{"disambiguationData":[OSD([sQuery(id+"F0.wireOp",EDGE,"E45")])],"isStart":false});
            var Q9;
            Q9=makeQuery(id+"F1.opExtrude","CAP_EDGE",EDGE,{"disambiguationData":[OSD([sQuery(id+"F0.wireOp",EDGE,"E6")])],"isStart":false});
            var Q10;
            Q10=makeQuery(id+"F1.opExtrude","CAP_EDGE",EDGE,{"disambiguationData":[OSD([sQuery(id+"F0.wireOp",EDGE,"E43")])],"isStart":false});
            var Q11;
            Q11=makeQuery(id+"F1.opExtrude","CAP_EDGE",EDGE,{"disambiguationData":[OSD([sQuery(id+"F0.wireOp",EDGE,"E7")])],"isStart":false});
            var Q12;
            Q12=makeQuery(id+"F1.opExtrude","CAP_EDGE",EDGE,{"disambiguationData":[OSD([sQuery(id+"F0.wireOp",EDGE,"E41")])],"isStart":false});
            var Q13;
            Q13=makeQuery(id+"F1.opExtrude","CAP_EDGE",EDGE,{"disambiguationData":[OSD([sQuery(id+"F0.wireOp",EDGE,"E8")])],"isStart":false});
            var Q14;
            Q14=makeQuery(id+"F1.opExtrude","CAP_EDGE",EDGE,{"disambiguationData":[OSD([sQuery(id+"F0.wireOp",EDGE,"E39")])],"isStart":false});
            var Q15;
            Q15=makeQuery(id+"F1.opExtrude","CAP_EDGE",EDGE,{"disambiguationData":[OSD([sQuery(id+"F0.wireOp",EDGE,"E13")])],"isStart":false});
            var Q16;
            Q16=makeQuery(id+"F1.opExtrude","CAP_EDGE",EDGE,{"disambiguationData":[OSD([sQuery(id+"F0.wireOp",EDGE,"E37")])],"isStart":false});
            var Q17;
            Q17=makeQuery(id+"F1.opExtrude","CAP_EDGE",EDGE,{"disambiguationData":[OSD([sQuery(id+"F0.wireOp",EDGE,"E9")])],"isStart":false});
            var Q18;
            Q18=makeQuery(id+"F1.opExtrude","CAP_EDGE",EDGE,{"disambiguationData":[OSD([sQuery(id+"F0.wireOp",EDGE,"E35")])],"isStart":false});
            var Q19;
            Q19=makeQuery(id+"F1.opExtrude","CAP_EDGE",EDGE,{"disambiguationData":[OSD([sQuery(id+"F0.wireOp",EDGE,"E10")])],"isStart":false});
            var Q20;
            Q20=makeQuery(id+"F1.opExtrude","CAP_EDGE",EDGE,{"disambiguationData":[OSD([sQuery(id+"F0.wireOp",EDGE,"E33")])],"isStart":false});
            var Q21;
            Q21=makeQuery(id+"F1.opExtrude","CAP_EDGE",EDGE,{"disambiguationData":[OSD([sQuery(id+"F0.wireOp",EDGE,"E11")])],"isStart":false});
            var Q22;
            Q22=makeQuery(id+"F1.opExtrude","CAP_EDGE",EDGE,{"disambiguationData":[OSD([sQuery(id+"F0.wireOp",EDGE,"E31")])],"isStart":false});
            var Q23;
            Q23=makeQuery(id+"F1.opExtrude","CAP_EDGE",EDGE,{"disambiguationData":[OSD([sQuery(id+"F0.wireOp",EDGE,"E12")])],"isStart":false});
            var Q24;
            {var subQ0=sQuery(id+"F0.wireOp",EDGE,"E3");Q24=makeQuery(id+"F1.opExtrude","CAP_EDGE",EDGE,{"disambiguationData":[OSD([subQ0]),TDD([makeQuery(id+"F0.imprint","IMPRINT",EDGE,{"disambiguationData":[TD([[makeQuery(id+"F0.imprint","INTERSECT",VERTEX,{"derivedFrom":[subQ0,sQuery(id+"F0.wireOp",EDGE,"E12"),sQuery(id+"F0.wireOp",EDGE,"E29")]}),1.0]])],"derivedFrom":subQ0})])],"isStart":false});}
            var Q25;
            {var subQ0=sQuery(id+"F0.wireOp",EDGE,"E3");Q25=makeQuery(id+"F1.opExtrude","CAP_EDGE",EDGE,{"disambiguationData":[OSD([subQ0]),TDD([makeQuery(id+"F0.imprint","IMPRINT",EDGE,{"disambiguationData":[TD([[makeQuery(id+"F0.imprint","INTERSECT",VERTEX,{"derivedFrom":[subQ0,sQuery(id+"F0.wireOp",EDGE,"E6"),sQuery(id+"F0.wireOp",EDGE,"E22")]}),1.0]])],"derivedFrom":subQ0})])],"isStart":false});}
            var Q26;
            {var subQ0=sQuery(id+"F0.wireOp",EDGE,"E3");Q26=makeQuery(id+"F1.opExtrude","CAP_EDGE",EDGE,{"disambiguationData":[OSD([subQ0]),TDD([makeQuery(id+"F0.imprint","IMPRINT",EDGE,{"disambiguationData":[TD([[makeQuery(id+"F0.imprint","INTERSECT",VERTEX,{"derivedFrom":[subQ0,sQuery(id+"F0.wireOp",EDGE,"E7"),sQuery(id+"F0.wireOp",EDGE,"E23")]}),1.0]])],"derivedFrom":subQ0})])],"isStart":false});}
            var Q27;
            {var subQ0=sQuery(id+"F0.wireOp",EDGE,"E3");Q27=makeQuery(id+"F1.opExtrude","CAP_EDGE",EDGE,{"disambiguationData":[OSD([subQ0]),TDD([makeQuery(id+"F0.imprint","IMPRINT",EDGE,{"disambiguationData":[TD([[makeQuery(id+"F0.imprint","INTERSECT",VERTEX,{"derivedFrom":[subQ0,sQuery(id+"F0.wireOp",EDGE,"E8"),sQuery(id+"F0.wireOp",EDGE,"E24")]}),1.0]])],"derivedFrom":subQ0})])],"isStart":false});}
            var Q28;
            {var subQ0=sQuery(id+"F0.wireOp",EDGE,"E3");Q28=makeQuery(id+"F1.opExtrude","CAP_EDGE",EDGE,{"disambiguationData":[OSD([subQ0]),TDD([makeQuery(id+"F0.imprint","IMPRINT",EDGE,{"disambiguationData":[TD([[makeQuery(id+"F0.imprint","INTERSECT",VERTEX,{"derivedFrom":[subQ0,sQuery(id+"F0.wireOp",EDGE,"E13"),sQuery(id+"F0.wireOp",EDGE,"E25")]}),1.0]])],"derivedFrom":subQ0})])],"isStart":false});}
            var Q29;
            {var subQ0=sQuery(id+"F0.wireOp",EDGE,"E3");Q29=makeQuery(id+"F1.opExtrude","CAP_EDGE",EDGE,{"disambiguationData":[OSD([subQ0]),TDD([makeQuery(id+"F0.imprint","IMPRINT",EDGE,{"disambiguationData":[TD([[makeQuery(id+"F0.imprint","INTERSECT",VERTEX,{"derivedFrom":[subQ0,sQuery(id+"F0.wireOp",EDGE,"E9"),sQuery(id+"F0.wireOp",EDGE,"E26")]}),1.0]])],"derivedFrom":subQ0})])],"isStart":false});}
            var Q30;
            {var subQ0=sQuery(id+"F0.wireOp",EDGE,"E3");Q30=makeQuery(id+"F1.opExtrude","CAP_EDGE",EDGE,{"disambiguationData":[OSD([subQ0]),TDD([makeQuery(id+"F0.imprint","IMPRINT",EDGE,{"disambiguationData":[TD([[makeQuery(id+"F0.imprint","INTERSECT",VERTEX,{"derivedFrom":[subQ0,sQuery(id+"F0.wireOp",EDGE,"E10"),sQuery(id+"F0.wireOp",EDGE,"E27")]}),1.0]])],"derivedFrom":subQ0})])],"isStart":false});}
            var Q31;
            {var subQ0=sQuery(id+"F0.wireOp",EDGE,"E3");Q31=makeQuery(id+"F1.opExtrude","CAP_EDGE",EDGE,{"disambiguationData":[OSD([subQ0]),TDD([makeQuery(id+"F0.imprint","IMPRINT",EDGE,{"disambiguationData":[TD([[makeQuery(id+"F0.imprint","INTERSECT",VERTEX,{"derivedFrom":[subQ0,sQuery(id+"F0.wireOp",EDGE,"E11"),sQuery(id+"F0.wireOp",EDGE,"E28")]}),1.0]])],"derivedFrom":subQ0})])],"isStart":false});}
            var Q32;
            {var subQ0=sQuery(id+"F0.wireOp",EDGE,"E4");Q32=makeQuery(id+"F1.opExtrude","CAP_EDGE",EDGE,{"disambiguationData":[OSD([subQ0]),TDD([makeQuery(id+"F0.imprint","IMPRINT",EDGE,{"disambiguationData":[TD([[makeQuery(id+"F0.imprint","INTERSECT",VERTEX,{"derivedFrom":[subQ0,sQuery(id+"F0.wireOp",EDGE,"E22")]}),1.0]])],"derivedFrom":subQ0})])],"isStart":false});}
            var Q33;
            {var subQ0=sQuery(id+"F0.wireOp",EDGE,"E4");Q33=makeQuery(id+"F1.opExtrude","CAP_EDGE",EDGE,{"disambiguationData":[OSD([subQ0]),TDD([makeQuery(id+"F0.imprint","IMPRINT",EDGE,{"disambiguationData":[TD([[makeQuery(id+"F0.imprint","INTERSECT",VERTEX,{"derivedFrom":[subQ0,sQuery(id+"F0.wireOp",EDGE,"E23")]}),1.0]])],"derivedFrom":subQ0})])],"isStart":false});}
            var Q34;
            {var subQ0=sQuery(id+"F0.wireOp",EDGE,"E4");Q34=makeQuery(id+"F1.opExtrude","CAP_EDGE",EDGE,{"disambiguationData":[OSD([subQ0]),TDD([makeQuery(id+"F0.imprint","IMPRINT",EDGE,{"disambiguationData":[TD([[makeQuery(id+"F0.imprint","INTERSECT",VERTEX,{"derivedFrom":[subQ0,sQuery(id+"F0.wireOp",EDGE,"E24")]}),1.0]])],"derivedFrom":subQ0})])],"isStart":false});}
            var Q35;
            {var subQ0=sQuery(id+"F0.wireOp",EDGE,"E4");Q35=makeQuery(id+"F1.opExtrude","CAP_EDGE",EDGE,{"disambiguationData":[OSD([subQ0]),TDD([makeQuery(id+"F0.imprint","IMPRINT",EDGE,{"disambiguationData":[TD([[makeQuery(id+"F0.imprint","INTERSECT",VERTEX,{"derivedFrom":[subQ0,sQuery(id+"F0.wireOp",EDGE,"E25")]}),1.0]])],"derivedFrom":subQ0})])],"isStart":false});}
            var Q36;
            {var subQ0=sQuery(id+"F0.wireOp",EDGE,"E4");Q36=makeQuery(id+"F1.opExtrude","CAP_EDGE",EDGE,{"disambiguationData":[OSD([subQ0]),TDD([makeQuery(id+"F0.imprint","IMPRINT",EDGE,{"disambiguationData":[TD([[makeQuery(id+"F0.imprint","INTERSECT",VERTEX,{"derivedFrom":[subQ0,sQuery(id+"F0.wireOp",EDGE,"E26")]}),1.0]])],"derivedFrom":subQ0})])],"isStart":false});}
            var Q37;
            {var subQ0=sQuery(id+"F0.wireOp",EDGE,"E4");Q37=makeQuery(id+"F1.opExtrude","CAP_EDGE",EDGE,{"disambiguationData":[OSD([subQ0]),TDD([makeQuery(id+"F0.imprint","IMPRINT",EDGE,{"disambiguationData":[TD([[makeQuery(id+"F0.imprint","INTERSECT",VERTEX,{"derivedFrom":[subQ0,sQuery(id+"F0.wireOp",EDGE,"E27")]}),1.0]])],"derivedFrom":subQ0})])],"isStart":false});}
            var Q38;
            {var subQ0=sQuery(id+"F0.wireOp",EDGE,"E4");Q38=makeQuery(id+"F1.opExtrude","CAP_EDGE",EDGE,{"disambiguationData":[OSD([subQ0]),TDD([makeQuery(id+"F0.imprint","IMPRINT",EDGE,{"disambiguationData":[TD([[makeQuery(id+"F0.imprint","INTERSECT",VERTEX,{"derivedFrom":[subQ0,sQuery(id+"F0.wireOp",EDGE,"E28")]}),1.0]])],"derivedFrom":subQ0})])],"isStart":false});}
            var Q39;
            {var subQ0=sQuery(id+"F0.wireOp",EDGE,"E4");Q39=makeQuery(id+"F1.opExtrude","CAP_EDGE",EDGE,{"disambiguationData":[OSD([subQ0]),TDD([makeQuery(id+"F0.imprint","IMPRINT",EDGE,{"disambiguationData":[TD([[makeQuery(id+"F0.imprint","INTERSECT",VERTEX,{"derivedFrom":[subQ0,sQuery(id+"F0.wireOp",EDGE,"E29")]}),1.0]])],"derivedFrom":subQ0})])],"isStart":false});}
            var Q40;
            Q40=makeQuery(id+"F1.opExtrude","CAP_EDGE",EDGE,{"disambiguationData":[OSD([sQuery(id+"F0.wireOp",EDGE,"E44")])],"isStart":false});
            var Q41;
            Q41=makeQuery(id+"F1.opExtrude","CAP_EDGE",EDGE,{"disambiguationData":[OSD([sQuery(id+"F0.wireOp",EDGE,"E42")])],"isStart":false});
            var Q42;
            Q42=makeQuery(id+"F1.opExtrude","CAP_EDGE",EDGE,{"disambiguationData":[OSD([sQuery(id+"F0.wireOp",EDGE,"E40")])],"isStart":false});
            var Q43;
            Q43=makeQuery(id+"F1.opExtrude","CAP_EDGE",EDGE,{"disambiguationData":[OSD([sQuery(id+"F0.wireOp",EDGE,"E38")])],"isStart":false});
            var Q44;
            Q44=makeQuery(id+"F1.opExtrude","CAP_EDGE",EDGE,{"disambiguationData":[OSD([sQuery(id+"F0.wireOp",EDGE,"E36")])],"isStart":false});
            var Q45;
            Q45=makeQuery(id+"F1.opExtrude","CAP_EDGE",EDGE,{"disambiguationData":[OSD([sQuery(id+"F0.wireOp",EDGE,"E34")])],"isStart":false});
            var Q46;
            Q46=makeQuery(id+"F1.opExtrude","CAP_EDGE",EDGE,{"disambiguationData":[OSD([sQuery(id+"F0.wireOp",EDGE,"E32")])],"isStart":false});
            var Q47;
            Q47=makeQuery(id+"F1.opExtrude","CAP_EDGE",EDGE,{"disambiguationData":[OSD([sQuery(id+"F0.wireOp",EDGE,"E30")])],"isStart":false});
            var Q48;
            Q48=makeQuery(id+"F1.opExtrude","CAP_EDGE",EDGE,{"disambiguationData":[OSD([sQuery(id+"F0.wireOp",EDGE,"E29")])],"isStart":false});
            var Q49;
            Q49=makeQuery(id+"F1.opExtrude","CAP_EDGE",EDGE,{"disambiguationData":[OSD([sQuery(id+"F0.wireOp",EDGE,"E22")])],"isStart":false});
            var Q50;
            Q50=makeQuery(id+"F1.opExtrude","CAP_EDGE",EDGE,{"disambiguationData":[OSD([sQuery(id+"F0.wireOp",EDGE,"E23")])],"isStart":false});
            var Q51;
            Q51=makeQuery(id+"F1.opExtrude","CAP_EDGE",EDGE,{"disambiguationData":[OSD([sQuery(id+"F0.wireOp",EDGE,"E24")])],"isStart":false});
            var Q52;
            Q52=makeQuery(id+"F1.opExtrude","CAP_EDGE",EDGE,{"disambiguationData":[OSD([sQuery(id+"F0.wireOp",EDGE,"E25")])],"isStart":false});
            var Q53;
            Q53=makeQuery(id+"F1.opExtrude","CAP_EDGE",EDGE,{"disambiguationData":[OSD([sQuery(id+"F0.wireOp",EDGE,"E26")])],"isStart":false});
            var Q54;
            Q54=makeQuery(id+"F1.opExtrude","CAP_EDGE",EDGE,{"disambiguationData":[OSD([sQuery(id+"F0.wireOp",EDGE,"E27")])],"isStart":false});
            var Q55;
            Q55=makeQuery(id+"F1.opExtrude","CAP_EDGE",EDGE,{"disambiguationData":[OSD([sQuery(id+"F0.wireOp",EDGE,"E28")])],"isStart":false});
            fillet(context, id + "F2", {"entities" : qUnion([Q0, Q1, Q2, Q3, Q4, Q5, Q6, Q7, Q8, Q9, Q10, Q11, Q12, Q13, Q14, Q15, Q16, Q17, Q18, Q19, Q20, Q21, Q22, Q23, Q24, Q25, Q26, Q27, Q28, Q29, Q30, Q31, Q32, Q33, Q34, Q35, Q36, Q37, Q38, Q39, Q40, Q41, Q42, Q43, Q44, Q45, Q46, Q47, Q48, Q49, Q50, Q51, Q52, Q53, Q54, Q55]), "radius" : 1 * mm, "tangentPropagation" : true, "allowEdgeOverflow" : false});
        }
    });
